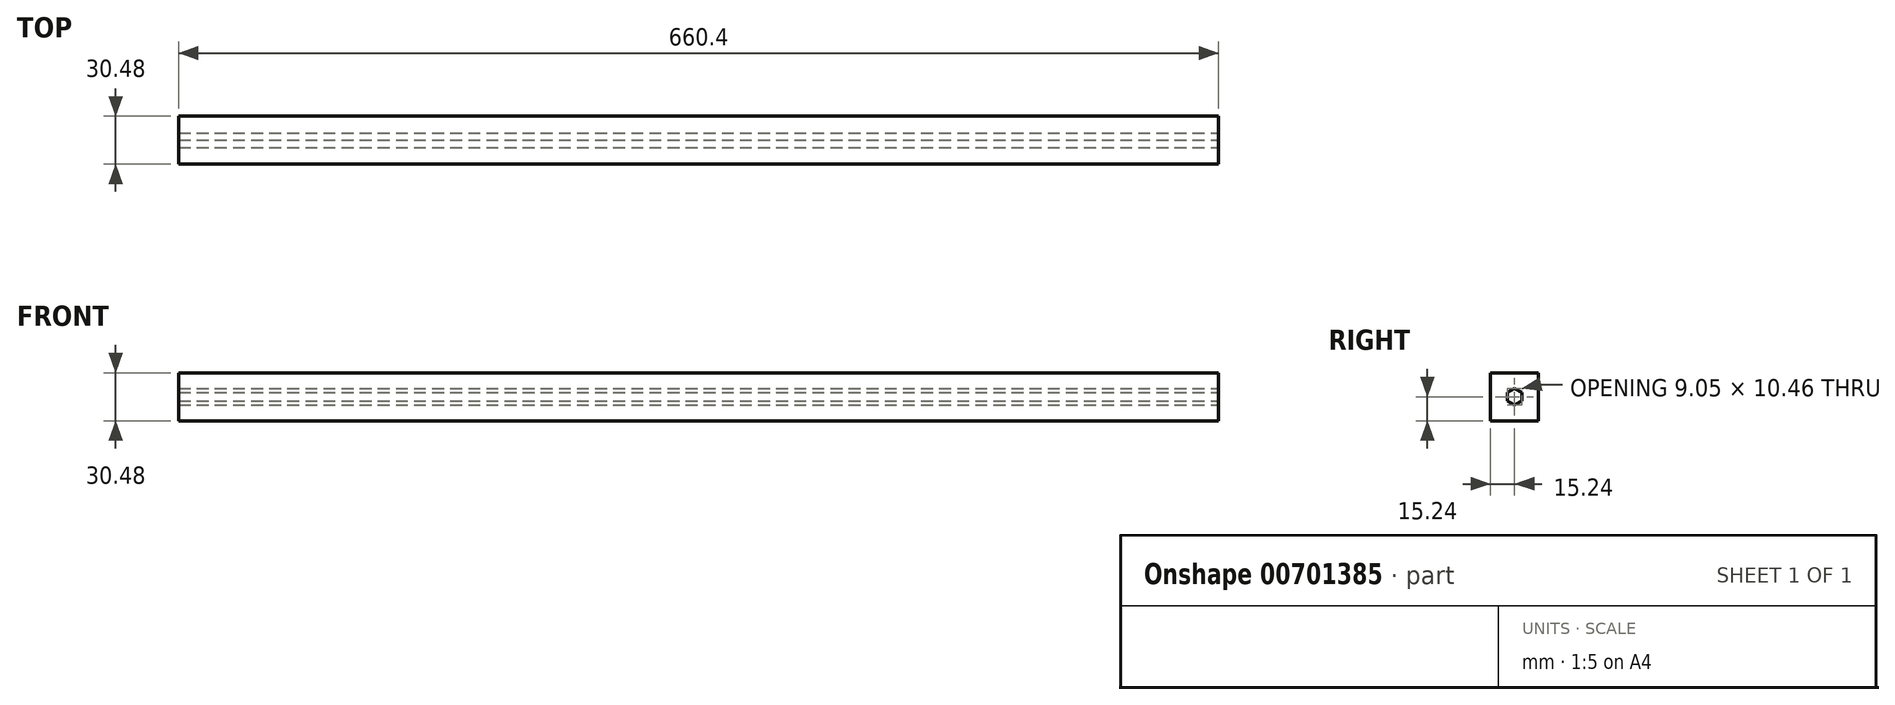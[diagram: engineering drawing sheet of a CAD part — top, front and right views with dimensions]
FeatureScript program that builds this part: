
annotation { "Feature Type Name" : "Feature", "Feature Type Description" : "" }
export const myFeature = defineFeature(function(context is Context, id is Id, definition is map)
    precondition{}
    {
        {
            var Q0;
            Q0=qCreatedBy(makeId("Right.planeOp"),FACE);
            var sketch = newSketch(context, id + "F0", { "sketchPlane" : qUnion([Q0])});
            skLineSegment(sketch, "E0.bottom", {"start": v(15.24, -15.24) * mm, "end": v(-15.24, -15.24) * mm});
            skLineSegment(sketch, "E0.top", {"start": v(15.24, 15.24) * mm, "end": v(-15.24, 15.24) * mm});
            skLineSegment(sketch, "E0.left", {"start": v(15.24, -15.24) * mm, "end": v(15.24, 15.24) * mm});
            skLineSegment(sketch, "E0.right", {"start": v(-15.24, -15.24) * mm, "end": v(-15.24, 15.24) * mm});
            skSolve(sketch);
        }
        {
            var Q0;
            Q0 = qSketchRegion(id + "F0", true);
            extrude(context, id + "F1", {"entities" : qUnion([Q0]), "endBound" : BoundingType.SYMMETRIC, "depth" : 660.4 * mm, "offsetDistance" : 25.4 * mm});
        }
        {
            var Q0;
            Q0=makeQuery(id+"F1.opExtrude","CAP_FACE",FACE,{"disambiguationData":[OSD([sQuery(id+"F0.wireOp",EDGE,"E0.bottom"),sQuery(id+"F0.wireOp",EDGE,"E0.top"),sQuery(id+"F0.wireOp",EDGE,"E0.left"),sQuery(id+"F0.wireOp",EDGE,"E0.right")])],"isStart":false});
            var sketch = newSketch(context, id + "F2", { "sketchPlane" : qUnion([Q0])});
            skCircle(sketch, "E1.cCircle", {"center": v(0, 0) * mm, "radius": 4.53 * mm, "construction": true});
            skLineSegment(sketch, "E1.0", {"start": v(4.53, 2.61) * mm, "end": v(4.53, -2.61) * mm});
            skLineSegment(sketch, "E1.1", {"start": v(4.53, -2.61) * mm, "end": v(0, -5.23) * mm});
            skLineSegment(sketch, "E1.2", {"start": v(0, -5.23) * mm, "end": v(-4.53, -2.61) * mm});
            skLineSegment(sketch, "E1.3", {"start": v(-4.53, -2.61) * mm, "end": v(-4.53, 2.61) * mm});
            skLineSegment(sketch, "E1.4", {"start": v(-4.53, 2.61) * mm, "end": v(0, 5.23) * mm});
            skLineSegment(sketch, "E1.5", {"start": v(0, 5.23) * mm, "end": v(4.53, 2.61) * mm});
            skPoint(sketch, "E1.0.midPoint", {"position": v(4.53, 0) * mm});
            skSolve(sketch);
        }
        {
            var Q0;
            Q0 = qSketchRegion(id + "F2", true);
            extrude(context, id + "F3", {"entities" : qUnion([Q0]), "operationType" : NewBodyOperationType.REMOVE, "endBound" : BoundingType.THROUGH_ALL, "oppositeDirection" : true, "depth" : 25.4 * mm, "offsetDistance" : 25.4 * mm});
        }
    });
